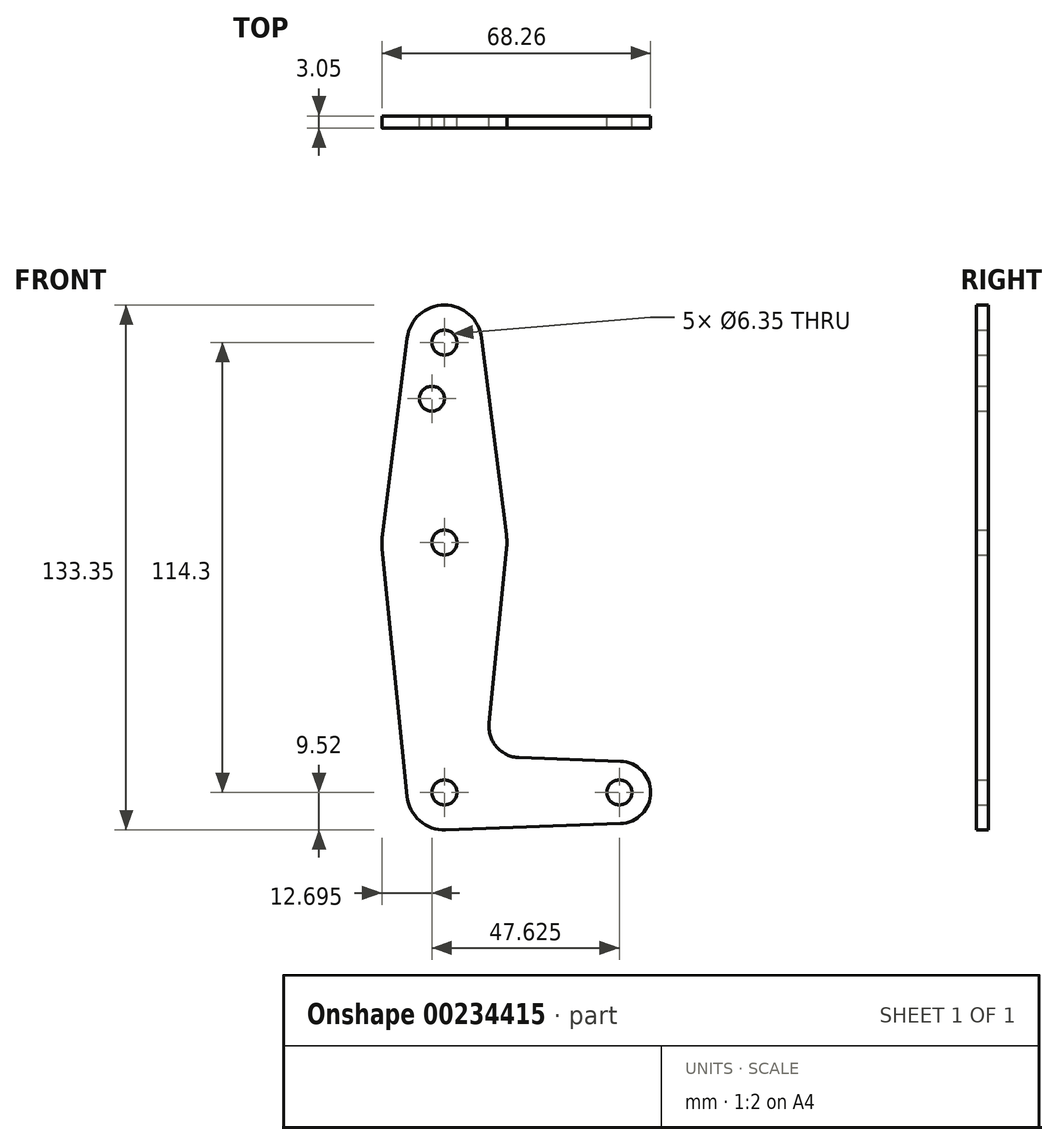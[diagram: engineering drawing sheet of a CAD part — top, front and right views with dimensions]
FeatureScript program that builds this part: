
annotation { "Feature Type Name" : "Feature", "Feature Type Description" : "" }
export const myFeature = defineFeature(function(context is Context, id is Id, definition is map)
    precondition{}
    {
        {
            var Q0;
            Q0=qCreatedBy(makeId("Front.planeOp"),FACE);
            var sketch = newSketch(context, id + "F0", { "sketchPlane" : qUnion([Q0])});
            skLineSegment(sketch, "E0", {"start": v(0, 114.3) * mm, "end": v(0, 0) * mm, "construction": true});
            skLineSegment(sketch, "E1", {"start": v(0, 0) * mm, "end": v(44.45, 0) * mm, "construction": true});
            skCircle(sketch, "E2", {"center": v(0, 114.3) * mm, "radius": 9.52 * mm});
            skCircle(sketch, "E3", {"center": v(44.45, 0) * mm, "radius": 7.94 * mm});
            skCircle(sketch, "E4", {"center": v(0, 0) * mm, "radius": 9.52 * mm});
            skCircle(sketch, "E5", {"center": v(0, 63.5) * mm, "radius": 15.88 * mm});
            skLineSegment(sketch, "E6", {"start": v(-9.45, 115.5) * mm, "end": v(-15.75, 65.48) * mm});
            skLineSegment(sketch, "E7", {"start": v(9.45, 115.5) * mm, "end": v(15.75, 65.48) * mm});
            skLineSegment(sketch, "E8", {"start": v(18.97, 8.85) * mm, "end": v(44.73, 7.93) * mm});
            skLineSegment(sketch, "E9", {"start": v(0.34, -9.52) * mm, "end": v(44.73, -7.93) * mm});
            skLineSegment(sketch, "E10", {"start": v(-15.8, 61.91) * mm, "end": v(-9.48, -0.95) * mm});
            skLineSegment(sketch, "E11", {"start": v(15.8, 61.91) * mm, "end": v(11.34, 17.6) * mm});
            skCircle(sketch, "E12", {"center": v(0, 114.3) * mm, "radius": 3.18 * mm});
            skCircle(sketch, "E13", {"center": v(-3.18, 100.03) * mm, "radius": 3.18 * mm});
            skCircle(sketch, "E14", {"center": v(0, 63.5) * mm, "radius": 3.18 * mm});
            skCircle(sketch, "E15", {"center": v(0, 0) * mm, "radius": 3.18 * mm});
            skCircle(sketch, "E16", {"center": v(44.45, 0) * mm, "radius": 3.18 * mm});
            skArc(sketch, "E17.filletArc", {"start": v(11.34, 17.6) * mm, "mid": v(13.26, 11.57) * mm, "end": v(18.97, 8.85) * mm});
            skSolve(sketch);
        }
        {
            var Q0;
            Q0 = qSketchRegion(id + "F0", true);
            extrude(context, id + "F1", {"entities" : qUnion([Q0]), "depth" : 3.05 * mm});
        }
    });
